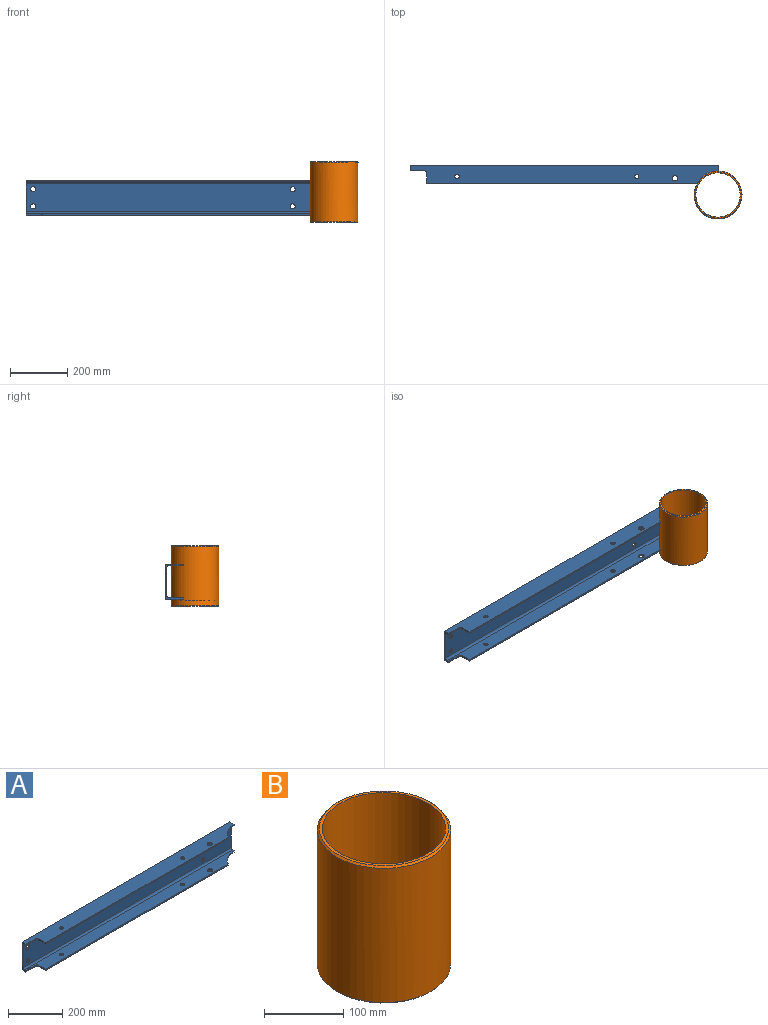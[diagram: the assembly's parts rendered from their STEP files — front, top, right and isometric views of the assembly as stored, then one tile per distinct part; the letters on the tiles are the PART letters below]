
ASSEMBLY  parts=2 mates=1
PART A: 30 faces, bbox 1080x65x125 mm
  f0: plane 1080x51.5mm, normal (0,0,-1), area 50026.5mm2, adj f3,f5,f7,f11,f13,f17,f18,f19
  f1: plane 1080x51.5mm, normal (0,0,1), area 50026.5mm2, adj f4,f5,f9,f11,f12,f14,f15,f16
  f2: plane 1080x65mm, normal (0,0,-1), area 64606.5mm2, adj f4,f5,f10,f11,f12,f14,f15,f16
  f3: plane 948.14x6mm, normal (0,-1,0), area 5688.8mm2, adj f0,f6,f13,f17
  f4: plane 948.14x6mm, normal (0,-1,0), area 5688.8mm2, adj f1,f2,f12,f15
  f5: plane 125x21mm, normal (1,0,0), area 954.1mm2, adj f0,f1,f2,f6,f7,f8,f9,f10
  f6: plane 1080x65mm, normal (0,0,1), area 64606.5mm2, adj f3,f5,f10,f11,f13,f17,f18,f19
  f7: cylinder r=7.5mm len=1080mm, axis (1,0,0), area 12723.5mm2, adj f0,f5,f8,f11
  f8: plane 1080x98mm, normal (0,-1,0), area 104822.1mm2, adj f5,f7,f9,f11,f26,f27,f28,f29
  f9: cylinder r=7.5mm len=1080mm, axis (1,0,0), area 12723.5mm2, adj f1,f5,f8,f11
  f10: plane 1080x125mm, normal (0,1,0), area 133982.1mm2, adj f2,f5,f6,f11,f26,f27,f28,f29
  f11: plane 125x20mm, normal (-1,0,0), area 942.1mm2, adj f0,f1,f2,f6,f7,f8,f9,f10
  f12: cylinder r=84mm len=73.86mm, axis (0,0,-1), area 541.5mm2, adj f1,f2,f4,f5
  f13: cylinder r=84mm len=73.86mm, axis (0,0,-1), area 541.5mm2, adj f0,f3,f5,f6
  f14: cylinder r=10mm len=10mm, axis (0,0,1), area 94.2mm2, adj f1,f2,f15,f16
  f15: plane 35x6mm, normal (-1,0,0), area 210mm2, adj f1,f2,f4,f14
  f16: plane 48x6mm, normal (0,-1,0), area 288mm2, adj f1,f2,f11,f14
  f17: plane 35x6mm, normal (-1,0,0), area 210mm2, adj f0,f3,f6,f18
  f18: cylinder r=10mm len=10mm, axis (0,0,1), area 94.2mm2, adj f0,f6,f17,f19
  f19: plane 48x6mm, normal (0,-1,0), area 288mm2, adj f0,f6,f11,f18
  f20: cylinder r=7.75mm len=15.5mm, axis (0,0,1), area 292.2mm2, adj f0,f6
  f21: cylinder r=7.75mm len=15.5mm, axis (0,0,1), area 292.2mm2, adj f0,f6
  f22: cylinder r=7.75mm len=15.5mm, axis (0,0,1), area 292.2mm2, adj f1,f2
  f23: cylinder r=7.75mm len=15.5mm, axis (0,0,1), area 292.2mm2, adj f1,f2
  f24: cylinder r=10mm len=20mm, axis (0,0,1), area 377mm2, adj f0,f6
  f25: cylinder r=10mm len=20mm, axis (0,0,1), area 377mm2, adj f1,f2
  f26: cylinder r=9mm len=18mm, axis (0,1,0), area 339.3mm2, adj f8,f10
  f27: cylinder r=9mm len=18mm, axis (0,1,0), area 339.3mm2, adj f8,f10
  f28: cylinder r=9mm len=18mm, axis (0,1,0), area 339.3mm2, adj f8,f10
  f29: cylinder r=9mm len=18mm, axis (0,1,0), area 339.3mm2, adj f8,f10
PART B: 8 faces, bbox 168x168x212 mm
  f0: plane 163x163mm, normal (0,0,1), area 1900.5mm2, adj f5,f7
  f1: cylinder r=84mm len=207mm, axis (0,0,-1), area 109252mm2, adj f6,f7
  f2: plane 163x163mm, normal (0,0,-1), area 761.1mm2, adj f3,f6
  f3: cylinder r=80mm len=160mm, axis (0,0,-1), area 10053.1mm2, adj f2,f4
  f4: plane 160x160mm, normal (0,0,-1), area 1139.5mm2, adj f3,f5
  f5: cylinder r=77.7mm len=192mm, axis (0,0,-1), area 93735.1mm2, adj f0,f4
  f6: cone r=81.5mm half-angle=45deg, axis (0,0,1), area 1838.2mm2, adj f1,f2
  f7: cone r=84mm half-angle=45deg, axis (0,0,-1), area 1838.2mm2, adj f0,f1
PLACE A t=(75.94,325.12,315.91)mm
PLACE B t=(75.94,325.12,315.91)mm
MATE fastened A.f12 <-> B.f1  axis (0,0,1) through (75.94,325.12,463.91)mm
